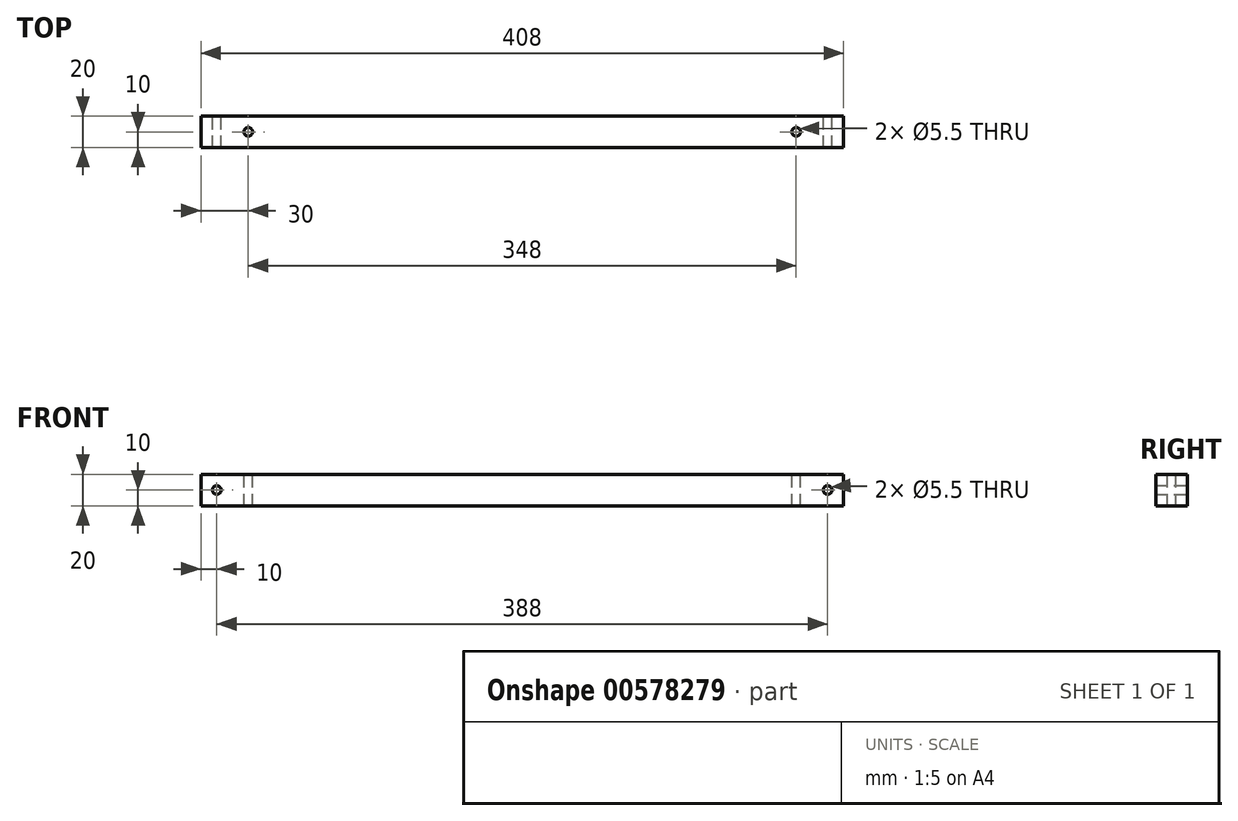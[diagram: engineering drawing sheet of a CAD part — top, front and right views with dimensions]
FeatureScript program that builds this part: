
annotation { "Feature Type Name" : "Feature", "Feature Type Description" : "" }
export const myFeature = defineFeature(function(context is Context, id is Id, definition is map)
    precondition{}
    {
        {
            var Q0;
            Q0=qCreatedBy(makeId("Front.planeOp"),FACE);
            var sketch = newSketch(context, id + "F0", { "sketchPlane" : qUnion([Q0])});
            skLineSegment(sketch, "E0.bottom", {"start": v(-204, 10) * mm, "end": v(204, 10) * mm});
            skLineSegment(sketch, "E0.top", {"start": v(-204, -10) * mm, "end": v(204, -10) * mm});
            skLineSegment(sketch, "E0.left", {"start": v(-204, 10) * mm, "end": v(-204, -10) * mm});
            skLineSegment(sketch, "E0.right", {"start": v(204, 10) * mm, "end": v(204, -10) * mm});
            skPoint(sketch, "E0.middle", {"position": v(0, 0) * mm});
            skCircle(sketch, "E1", {"center": v(-194, 0) * mm, "radius": 2.75 * mm});
            skPoint(sketch, "E1.centerSnap0", {"position": v(-204, 0) * mm});
            skCircle(sketch, "E2", {"center": v(194, 0) * mm, "radius": 2.75 * mm});
            skPoint(sketch, "E2.centerSnap0", {"position": v(204, 0) * mm});
            skSolve(sketch);
        }
        {
            var Q0;
            Q0 = qSketchRegion(id + "F0", true);
            extrude(context, id + "F1", {"entities" : qUnion([Q0]), "depth" : 20 * mm, "offsetDistance" : 25 * mm});
        }
        {
            var Q0;
            Q0=makeQuery(id+"F1.opExtrude","SWEPT_FACE",FACE,{"disambiguationData":[OSD([sQuery(id+"F0.wireOp",EDGE,"E0.bottom")])]});
            var sketch = newSketch(context, id + "F2", { "sketchPlane" : qUnion([Q0])});
            skCircle(sketch, "E3", {"center": v(-174, -10) * mm, "radius": 2.75 * mm});
            skPoint(sketch, "E3.centerSnap0", {"position": v(-204, -10) * mm});
            skCircle(sketch, "E4", {"center": v(174, -10) * mm, "radius": 2.75 * mm});
            skPoint(sketch, "E4.centerSnap0", {"position": v(204, -10) * mm});
            skSolve(sketch);
        }
        {
            var Q0;
            Q0 = qSketchRegion(id + "F2", true);
            extrude(context, id + "F3", {"entities" : qUnion([Q0]), "operationType" : NewBodyOperationType.REMOVE, "oppositeDirection" : true, "depth" : 20 * mm, "offsetDistance" : 25 * mm});
        }
    });
